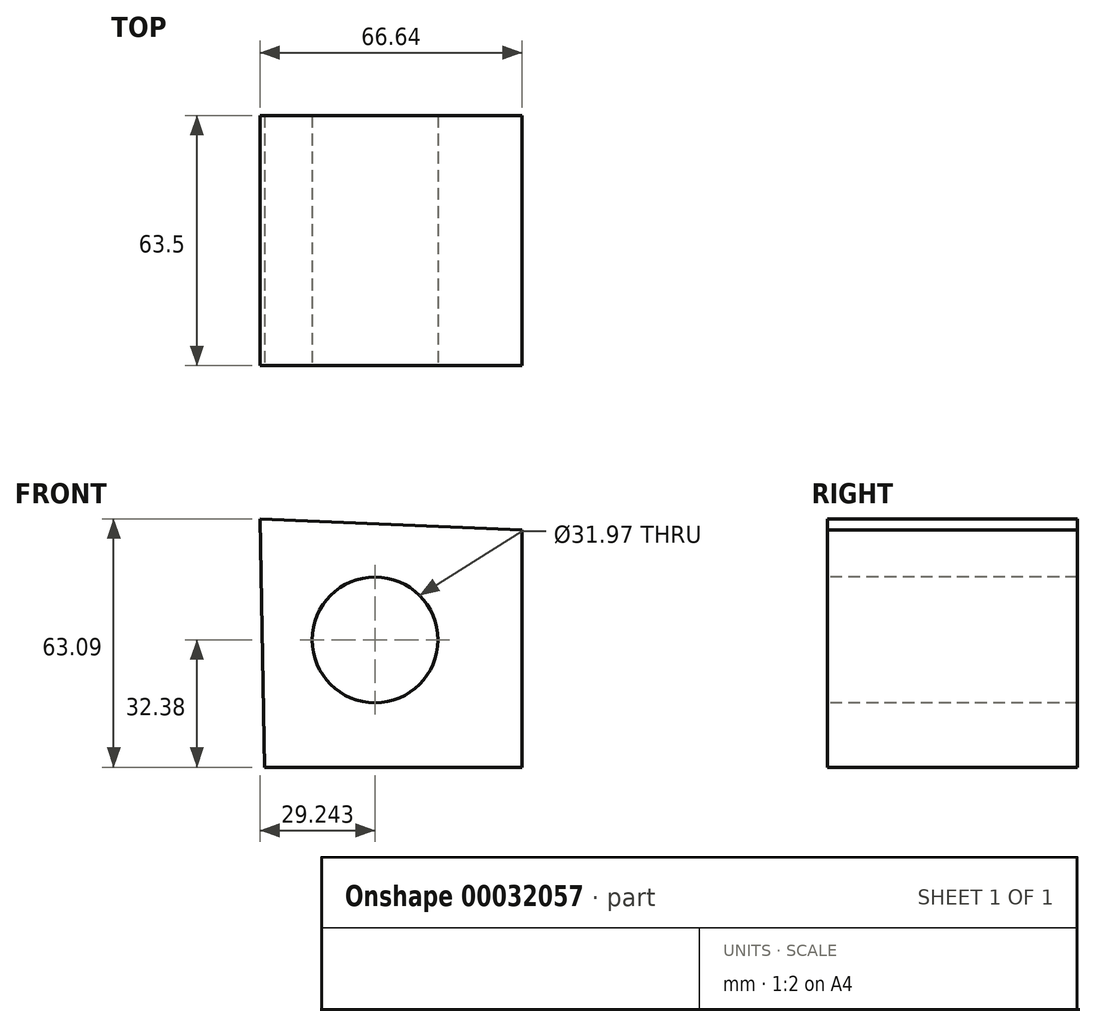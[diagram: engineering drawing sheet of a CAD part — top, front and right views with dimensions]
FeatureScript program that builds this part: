
annotation { "Feature Type Name" : "Feature", "Feature Type Description" : "" }
export const myFeature = defineFeature(function(context is Context, id is Id, definition is map)
    precondition{}
    {
        {
            var Q0;
            Q0=qCreatedBy(makeId("Front.planeOp"),FACE);
            var sketch = newSketch(context, id + "F0", { "sketchPlane" : qUnion([Q0])});
            skLineSegment(sketch, "E0", {"start": v(-60.2, 44.49) * mm, "end": v(6.44, 41.76) * mm});
            skLineSegment(sketch, "E1", {"start": v(6.44, 41.76) * mm, "end": v(6.44, -18.6) * mm});
            skLineSegment(sketch, "E2", {"start": v(6.44, -18.6) * mm, "end": v(-59.06, -18.6) * mm});
            skLineSegment(sketch, "E3", {"start": v(-59.06, -18.6) * mm, "end": v(-60.2, 44.49) * mm});
            skSolve(sketch);
        }
        {
            var Q0;
            Q0=makeQuery(id+"F0.imprint","IMPRINT",FACE,{"disambiguationData":[TD([[makeQuery(id+"F0.imprint","IMPRINT",EDGE,{"derivedFrom":sQuery(id+"F0.wireOp",EDGE,"E0")}),-1.0]])]});
            extrude(context, id + "F1", {"entities" : qUnion([Q0]), "oppositeDirection" : true, "depth" : 63.5 * mm});
        }
        {
            var Q0;
            Q0=makeQuery(id+"F1.opExtrude","CAP_FACE",FACE,{"disambiguationData":[OSD([sQuery(id+"F0.wireOp",EDGE,"E0"),sQuery(id+"F0.wireOp",EDGE,"E1"),sQuery(id+"F0.wireOp",EDGE,"E2"),sQuery(id+"F0.wireOp",EDGE,"E3")])],"isStart":true});
            var sketch = newSketch(context, id + "F2", { "sketchPlane" : qUnion([Q0])});
            skCircle(sketch, "E4", {"center": v(-30.96, 13.78) * mm, "radius": 15.98 * mm});
            skSolve(sketch);
        }
        {
            var Q0;
            Q0=makeQuery(id+"F2.imprint","IMPRINT",FACE,{"disambiguationData":[TD([[makeQuery(id+"F2.imprint","IMPRINT",EDGE,{"derivedFrom":sQuery(id+"F2.wireOp",EDGE,"E4")}),1.0]])]});
            extrude(context, id + "F3", {"entities" : qUnion([Q0]), "operationType" : NewBodyOperationType.REMOVE, "endBound" : BoundingType.THROUGH_ALL, "oppositeDirection" : true, "depth" : 25.4 * mm});
        }
    });
